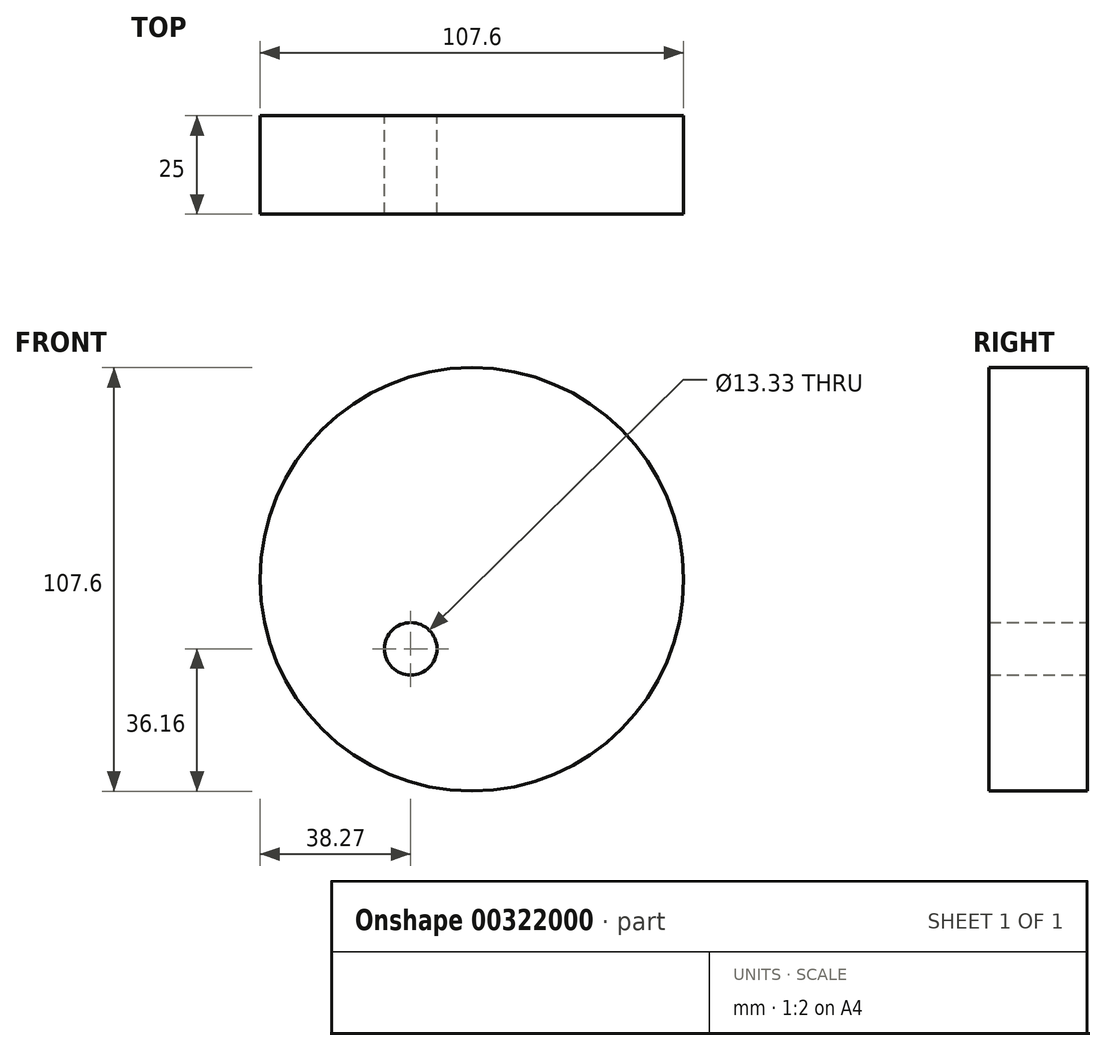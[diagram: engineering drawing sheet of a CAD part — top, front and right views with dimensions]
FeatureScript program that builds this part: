
annotation { "Feature Type Name" : "Feature", "Feature Type Description" : "" }
export const myFeature = defineFeature(function(context is Context, id is Id, definition is map)
    precondition{}
    {
        {
            var Q0;
            Q0=qCreatedBy(makeId("Front.planeOp"),FACE);
            var sketch = newSketch(context, id + "F0", { "sketchPlane" : qUnion([Q0])});
            skCircle(sketch, "E0", {"center": v(0, 0) * mm, "radius": 6.66 * mm});
            skCircle(sketch, "E1", {"center": v(15.53, 17.64) * mm, "radius": 53.8 * mm});
            skSolve(sketch);
        }
        {
            var Q0;
            Q0 = qSketchRegion(id + "F0", true);
            extrude(context, id + "F1", {"entities" : qUnion([Q0]), "depth" : 25 * mm});
        }
    });
